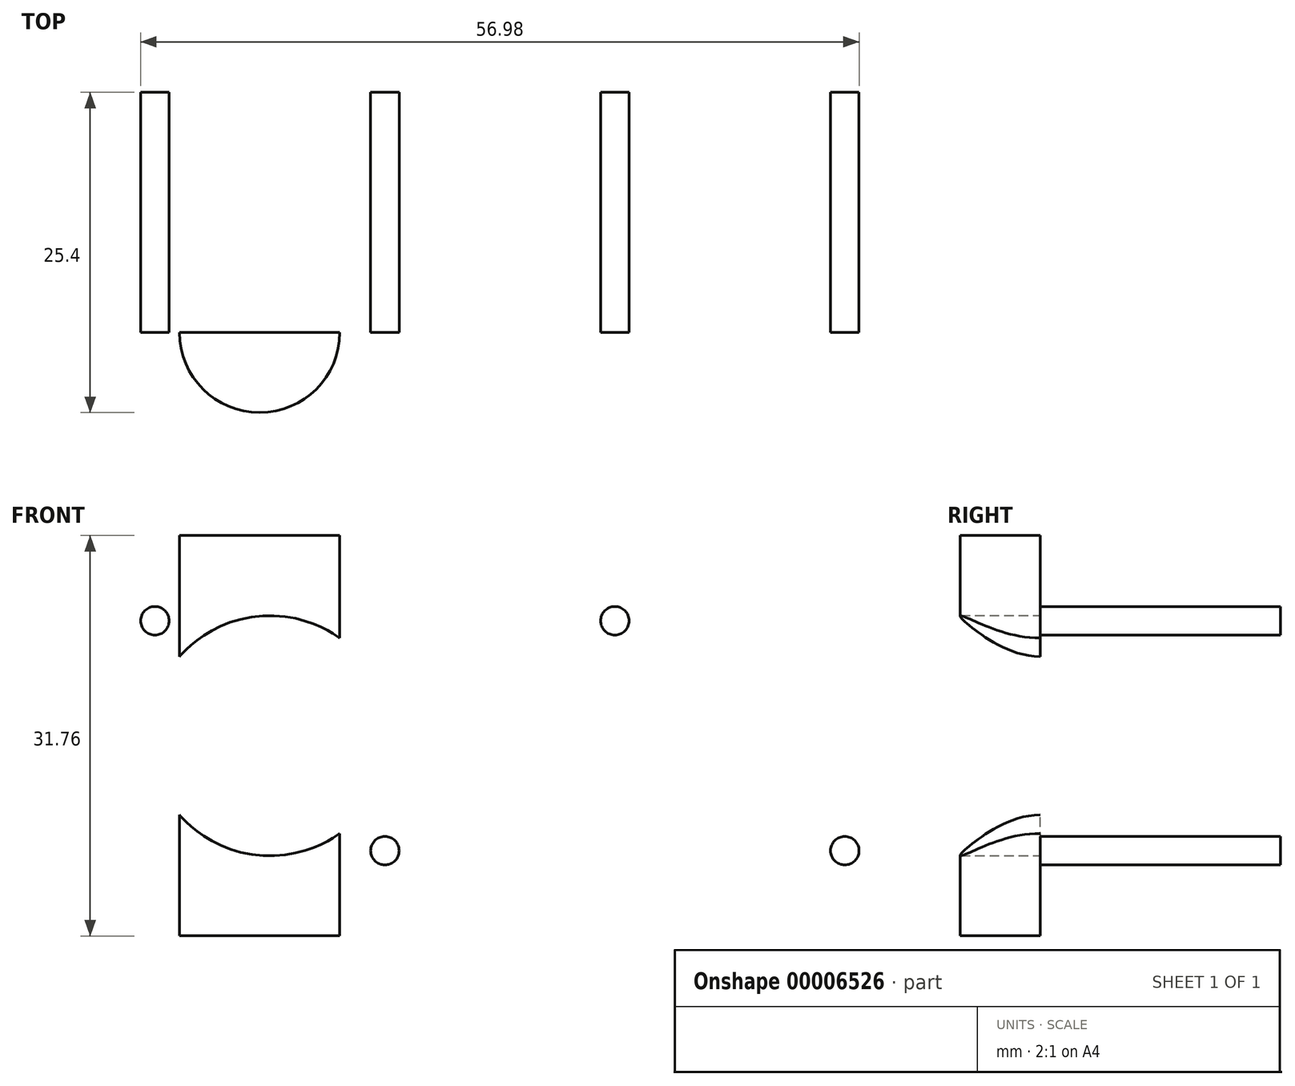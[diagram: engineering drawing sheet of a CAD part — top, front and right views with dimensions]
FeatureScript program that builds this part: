
annotation { "Feature Type Name" : "Feature", "Feature Type Description" : "" }
export const myFeature = defineFeature(function(context is Context, id is Id, definition is map)
    precondition{}
    {
        {
            var Q0;
            Q0=qCreatedBy(makeId("Front.planeOp"),FACE);
            var sketch = newSketch(context, id + "F0", { "sketchPlane" : qUnion([Q0])});
            skLineSegment(sketch, "E0.rect.bottom", {"start": v(31.75, 15.88) * mm, "end": v(-31.75, 15.87) * mm});
            skLineSegment(sketch, "E0.rect.top", {"start": v(31.75, -15.88) * mm, "end": v(-31.75, -15.88) * mm});
            skLineSegment(sketch, "E0.rect.left", {"start": v(31.75, 15.87) * mm, "end": v(31.75, -15.88) * mm});
            skLineSegment(sketch, "E0.rect.right", {"start": v(-31.75, 15.87) * mm, "end": v(-31.75, -15.88) * mm});
            skPoint(sketch, "E0.rect.middle", {"position": v(0, 0) * mm});
            skSolve(sketch);
        }
        {
            var Q0;
            Q0 = qSketchRegion(id + "F0", true);
            extrude(context, id + "F1", {"entities" : qUnion([Q0]), "oppositeDirection" : true, "depth" : 38.1 * mm});
        }
        {
            var Q0;
            Q0=qCreatedBy(makeId("Front.planeOp"),FACE);
            var sketch = newSketch(context, id + "F2", { "sketchPlane" : qUnion([Q0])});
            skCircle(sketch, "E1", {"center": v(0, 0) * mm, "radius": 9.53 * mm});
            skLineSegment(sketch, "E2", {"start": v(9.12, 19.77) * mm, "end": v(9.12, -18.73) * mm, "construction": true});
            skLineSegment(sketch, "E3", {"start": v(-35.9, 9.12) * mm, "end": v(34.92, 9.12) * mm, "construction": true});
            skCircle(sketch, "E4", {"center": v(9.12, 9.12) * mm, "radius": 1.13 * mm});
            skCircle(sketch, "E5.0.MirrorC", {"center": v(-9.12, 9.12) * mm, "radius": 1.13 * mm});
            skCircle(sketch, "E6.0.MirrorC", {"center": v(-9.12, -9.12) * mm, "radius": 1.13 * mm});
            skCircle(sketch, "E7.0.MirrorC", {"center": v(9.12, -9.12) * mm, "radius": 1.13 * mm});
            skLineSegment(sketch, "E8", {"start": v(34.75, 0) * mm, "end": v(-37.08, 0) * mm, "construction": true});
            skSolve(sketch);
        }
        {
            var Q0;
            Q0=makeQuery(id+"F2.imprint","IMPRINT",FACE,{"disambiguationData":[TD([[makeQuery(id+"F2.imprint","IMPRINT",EDGE,{"derivedFrom":sQuery(id+"F2.wireOp",EDGE,"E5.0.MirrorC")}),-1.0]])]});
            var Q1;
            Q1=makeQuery(id+"F2.imprint","IMPRINT",FACE,{"disambiguationData":[TD([[makeQuery(id+"F2.imprint","IMPRINT",EDGE,{"derivedFrom":sQuery(id+"F2.wireOp",EDGE,"E4")}),1.0]])]});
            var Q2;
            Q2=makeQuery(id+"F2.imprint","IMPRINT",FACE,{"disambiguationData":[TD([[makeQuery(id+"F2.imprint","IMPRINT",EDGE,{"derivedFrom":sQuery(id+"F2.wireOp",EDGE,"E7.0.MirrorC")}),-1.0]])]});
            var Q3;
            Q3=makeQuery(id+"F2.imprint","IMPRINT",FACE,{"disambiguationData":[TD([[makeQuery(id+"F2.imprint","IMPRINT",EDGE,{"derivedFrom":sQuery(id+"F2.wireOp",EDGE,"E6.0.MirrorC")}),1.0]])]});
            extrude(context, id + "F3", {"entities" : qUnion([Q0, Q1, Q2, Q3]), "operationType" : NewBodyOperationType.REMOVE, "oppositeDirection" : true, "depth" : 19.05 * mm});
        }
        {
            var Q0;
            Q0=makeQuery(id+"F2.imprint","IMPRINT",FACE,{"disambiguationData":[TD([[makeQuery(id+"F2.imprint","IMPRINT",EDGE,{"derivedFrom":sQuery(id+"F2.wireOp",EDGE,"E1")}),1.0]])]});
            extrude(context, id + "F4", {"entities" : qUnion([Q0]), "operationType" : NewBodyOperationType.REMOVE, "oppositeDirection" : true, "depth" : 25.4 * mm});
        }
        {
            var Q0;
            Q0=makeQuery(id+"F1.opExtrude","CAP_FACE",FACE,{"disambiguationData":[OSD([sQuery(id+"F0.wireOp",EDGE,"E0.rect.bottom"),sQuery(id+"F0.wireOp",EDGE,"E0.rect.top"),sQuery(id+"F0.wireOp",EDGE,"E0.rect.left"),sQuery(id+"F0.wireOp",EDGE,"E0.rect.right")])],"isStart":false});
            var sketch = newSketch(context, id + "F5", { "sketchPlane" : qUnion([Q0])});
            skCircle(sketch, "E9", {"center": v(-18.24, 0) * mm, "radius": 9.53 * mm});
            skCircle(sketch, "E10", {"center": v(18.24, 0) * mm, "radius": 9.53 * mm});
            skLineSegment(sketch, "E11", {"start": v(-18.24, 19.84) * mm, "end": v(-18.24, -19.84) * mm, "construction": true});
            skLineSegment(sketch, "E12", {"start": v(18.24, 19.94) * mm, "end": v(18.24, -22.68) * mm, "construction": true});
            skLineSegment(sketch, "E13", {"start": v(9.12, 20.55) * mm, "end": v(9.12, -25.17) * mm, "construction": true});
            skLineSegment(sketch, "E14", {"start": v(-9.12, 19.78) * mm, "end": v(-9.12, -25.68) * mm, "construction": true});
            skLineSegment(sketch, "E15", {"start": v(-34.42, 9.12) * mm, "end": v(37.28, 9.12) * mm, "construction": true});
            skCircle(sketch, "E16", {"center": v(9.12, 9.12) * mm, "radius": 1.13 * mm});
            skCircle(sketch, "E17.0.MirrorC", {"center": v(27.36, 9.12) * mm, "radius": 1.13 * mm});
            skCircle(sketch, "E18.0.MirrorC", {"center": v(-9.12, 9.12) * mm, "radius": 1.13 * mm});
            skCircle(sketch, "E19.0.MirrorC", {"center": v(-27.36, 9.12) * mm, "radius": 1.13 * mm});
            skCircle(sketch, "E20.0.MirrorC", {"center": v(-27.36, -9.12) * mm, "radius": 1.13 * mm});
            skCircle(sketch, "E21.0.MirrorC", {"center": v(-9.12, -9.12) * mm, "radius": 1.13 * mm});
            skCircle(sketch, "E22.0.MirrorC", {"center": v(9.12, -9.12) * mm, "radius": 1.13 * mm});
            skCircle(sketch, "E23.0.MirrorC", {"center": v(27.36, -9.12) * mm, "radius": 1.13 * mm});
            skSolve(sketch);
        }
        {
            var Q0;
            Q0=makeQuery(id+"F5.imprint","IMPRINT",FACE,{"disambiguationData":[TD([[makeQuery(id+"F5.imprint","IMPRINT",EDGE,{"derivedFrom":sQuery(id+"F5.wireOp",EDGE,"E9")}),1.0]])]});
            var Q1;
            Q1=makeQuery(id+"F5.imprint","IMPRINT",FACE,{"disambiguationData":[TD([[makeQuery(id+"F5.imprint","IMPRINT",EDGE,{"derivedFrom":sQuery(id+"F5.wireOp",EDGE,"E10")}),1.0]])]});
            var Q2;
            Q2=sQuery(id+"F5.wireOp",EDGE,"E9");
            var Q3;
            Q3=sQuery(id+"F5.wireOp",EDGE,"E10");
            extrude(context, id + "F6", {"entities" : qUnion([Q0, Q1]), "operationType" : NewBodyOperationType.REMOVE, "surfaceEntities" : qUnion([Q2, Q3]), "oppositeDirection" : true, "depth" : 25.4 * mm});
        }
        {
            var Q0;
            Q0=makeQuery(id+"F5.imprint","IMPRINT",FACE,{"disambiguationData":[TD([[makeQuery(id+"F5.imprint","IMPRINT",EDGE,{"derivedFrom":sQuery(id+"F5.wireOp",EDGE,"E19.0.MirrorC")}),1.0]])]});
            var Q1;
            Q1=makeQuery(id+"F5.imprint","IMPRINT",FACE,{"disambiguationData":[TD([[makeQuery(id+"F5.imprint","IMPRINT",EDGE,{"derivedFrom":sQuery(id+"F5.wireOp",EDGE,"E18.0.MirrorC")}),-1.0]])]});
            var Q2;
            Q2=makeQuery(id+"F5.imprint","IMPRINT",FACE,{"disambiguationData":[TD([[makeQuery(id+"F5.imprint","IMPRINT",EDGE,{"derivedFrom":sQuery(id+"F5.wireOp",EDGE,"E16")}),1.0]])]});
            var Q3;
            Q3=makeQuery(id+"F5.imprint","IMPRINT",FACE,{"disambiguationData":[TD([[makeQuery(id+"F5.imprint","IMPRINT",EDGE,{"derivedFrom":sQuery(id+"F5.wireOp",EDGE,"E17.0.MirrorC")}),-1.0]])]});
            var Q4;
            Q4=makeQuery(id+"F5.imprint","IMPRINT",FACE,{"disambiguationData":[TD([[makeQuery(id+"F5.imprint","IMPRINT",EDGE,{"derivedFrom":sQuery(id+"F5.wireOp",EDGE,"E23.0.MirrorC")}),1.0]])]});
            var Q5;
            Q5=makeQuery(id+"F5.imprint","IMPRINT",FACE,{"disambiguationData":[TD([[makeQuery(id+"F5.imprint","IMPRINT",EDGE,{"derivedFrom":sQuery(id+"F5.wireOp",EDGE,"E22.0.MirrorC")}),-1.0]])]});
            var Q6;
            Q6=makeQuery(id+"F5.imprint","IMPRINT",FACE,{"disambiguationData":[TD([[makeQuery(id+"F5.imprint","IMPRINT",EDGE,{"derivedFrom":sQuery(id+"F5.wireOp",EDGE,"E21.0.MirrorC")}),1.0]])]});
            var Q7;
            Q7=makeQuery(id+"F5.imprint","IMPRINT",FACE,{"disambiguationData":[TD([[makeQuery(id+"F5.imprint","IMPRINT",EDGE,{"derivedFrom":sQuery(id+"F5.wireOp",EDGE,"E20.0.MirrorC")}),-1.0]])]});
            var Q8;
            Q8=sQuery(id+"F5.wireOp",EDGE,"E19.0.MirrorC");
            var Q9;
            Q9=sQuery(id+"F5.wireOp",EDGE,"E18.0.MirrorC");
            var Q10;
            Q10=sQuery(id+"F5.wireOp",EDGE,"E16");
            var Q11;
            Q11=sQuery(id+"F5.wireOp",EDGE,"E17.0.MirrorC");
            var Q12;
            Q12=sQuery(id+"F5.wireOp",EDGE,"E23.0.MirrorC");
            var Q13;
            Q13=sQuery(id+"F5.wireOp",EDGE,"E22.0.MirrorC");
            var Q14;
            Q14=sQuery(id+"F2.wireOp",EDGE,"E7.0.MirrorC");
            var Q15;
            Q15=sQuery(id+"F5.wireOp",EDGE,"E20.0.MirrorC");
            extrude(context, id + "F7", {"entities" : qUnion([Q0, Q1, Q2, Q3, Q4, Q5, Q6, Q7]), "operationType" : NewBodyOperationType.REMOVE, "surfaceEntities" : qUnion([Q8, Q9, Q10, Q11, Q12, Q13, Q14, Q15]), "oppositeDirection" : true, "depth" : 19.05 * mm});
        }
        {
            var Q0;
            Q0=makeQuery(id+"F5.imprint","IMPRINT",FACE,{"disambiguationData":[TD([[makeQuery(id+"F5.imprint","IMPRINT",EDGE,{"derivedFrom":sQuery(id+"F5.wireOp",EDGE,"E9")}),-1.0]])]});
            var sketch = newSketch(context, id + "F8", { "sketchPlane" : qUnion([Q0])});
            skSolve(sketch);
        }
        {
            var Q0;
            Q0=makeQuery(id+"F1.opExtrude","SWEPT_FACE",FACE,{"disambiguationData":[OSD([sQuery(id+"F0.wireOp",EDGE,"E0.rect.bottom")])]});
            var sketch = newSketch(context, id + "F9", { "sketchPlane" : qUnion([Q0])});
            skLineSegment(sketch, "E24", {"start": v(31.75, 19.05) * mm, "end": v(-31.75, 19.05) * mm, "construction": true});
            skCircle(sketch, "E25", {"center": v(19.05, 19.05) * mm, "radius": 6.35 * mm});
            skCircle(sketch, "E26.0.MirrorC", {"center": v(-19.05, 19.05) * mm, "radius": 6.35 * mm});
            skSolve(sketch);
        }
        {
            var Q0;
            Q0=makeQuery(id+"F9.imprint","IMPRINT",FACE,{"disambiguationData":[TD([[makeQuery(id+"F9.imprint","IMPRINT",EDGE,{"derivedFrom":sQuery(id+"F9.wireOp",EDGE,"E26.0.MirrorC")}),-1.0]])]});
            var Q1;
            Q1=makeQuery(id+"F9.imprint","IMPRINT",FACE,{"disambiguationData":[TD([[makeQuery(id+"F9.imprint","IMPRINT",EDGE,{"derivedFrom":sQuery(id+"F9.wireOp",EDGE,"E25")}),1.0]])]});
            var Q2;
            Q2 = qSketchRegion(id + "F8", true);
            extrude(context, id + "F10", {"entities" : qUnion([Q0, Q1, Q2]), "operationType" : NewBodyOperationType.REMOVE, "oppositeDirection" : true, "depth" : 31.75 * mm});
        }
    });
